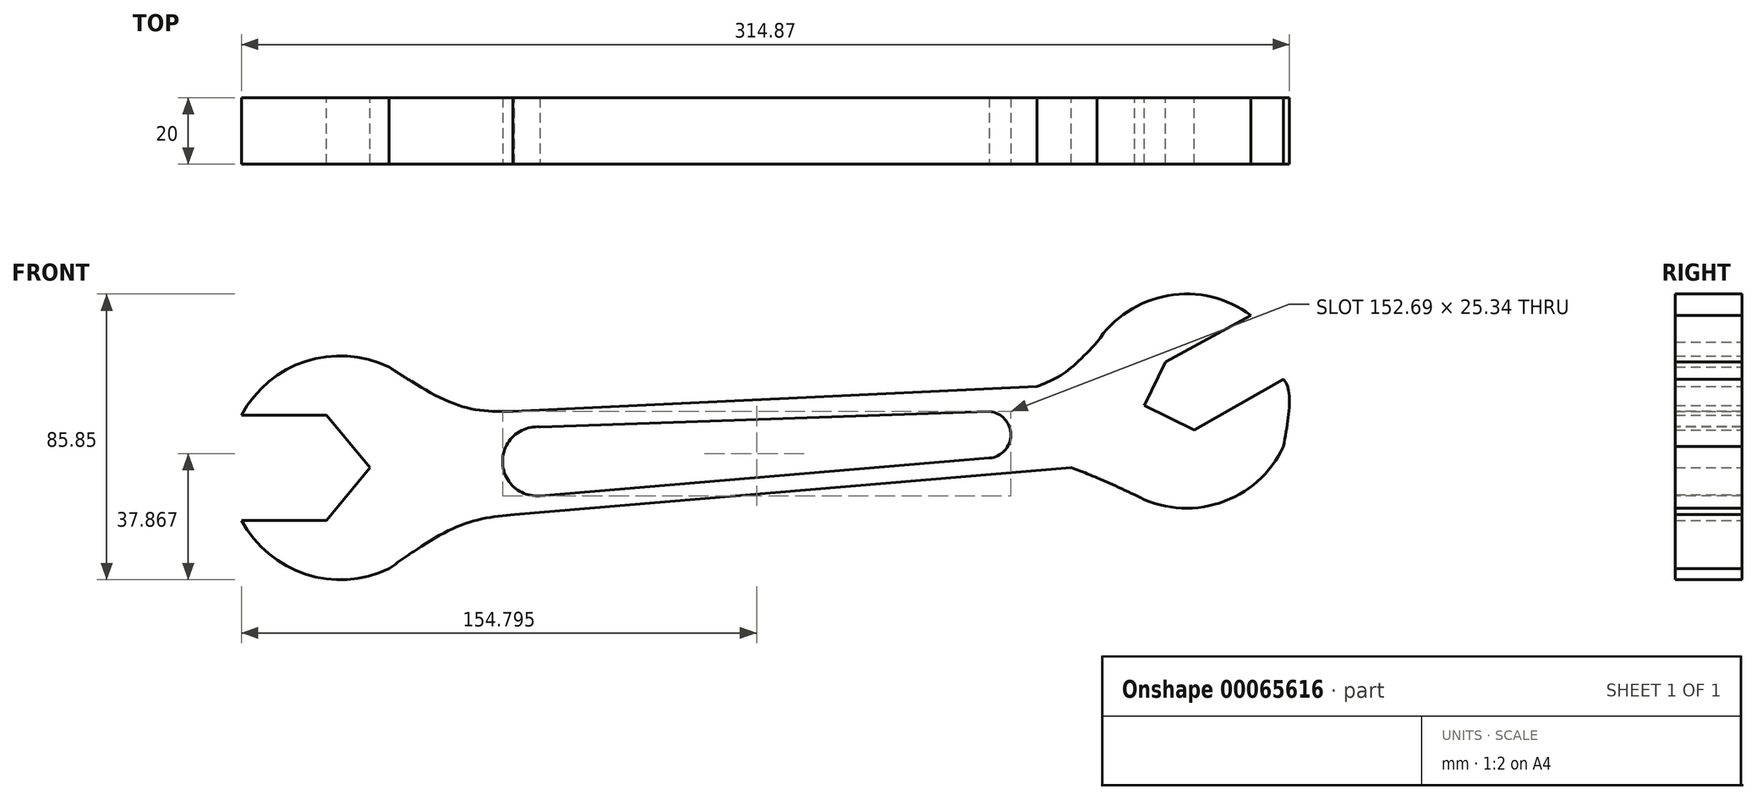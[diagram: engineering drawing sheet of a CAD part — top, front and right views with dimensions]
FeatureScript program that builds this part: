
annotation { "Feature Type Name" : "Feature", "Feature Type Description" : "" }
export const myFeature = defineFeature(function(context is Context, id is Id, definition is map)
    precondition{}
    {
        {
            var Q0;
            Q0=qCreatedBy(makeId("Front.planeOp"),FACE);
            var sketch = newSketch(context, id + "F0", { "sketchPlane" : qUnion([Q0])});
            skLineSegment(sketch, "E0", {"start": v(-115.15, 15.74) * mm, "end": v(-89.65, 15.74) * mm});
            skLineSegment(sketch, "E1", {"start": v(-89.65, 15.74) * mm, "end": v(-76.58, 0) * mm});
            skLineSegment(sketch, "E2", {"start": v(-76.58, 0) * mm, "end": v(-89.65, -15.82) * mm});
            skLineSegment(sketch, "E3", {"start": v(-89.65, -15.82) * mm, "end": v(-115.15, -15.82) * mm});
            skArc(sketch, "E4", {"start": v(-115.15, -15.82) * mm, "mid": v(-51.82, -0.04) * mm, "end": v(-115.15, 15.74) * mm});
            skFitSpline(sketch, "E5", {"points": [v(-70.8, 30.24) * mm, v(-49.2, 18.47) * mm, v(-33.55, 16.87) * mm], "startDerivative": vector(39.91, -26.01) * mm, "endDerivative": vector(34.43, 0.28) * mm});
            skFitSpline(sketch, "E6", {"points": [v(-70.8, -30.31) * mm, v(-49.2, -17.27) * mm, v(-33.14, -14.06) * mm], "startDerivative": vector(39.83, 28.07) * mm, "endDerivative": vector(35.33, 3.55) * mm});
            skLineSegment(sketch, "E7", {"start": v(-33.55, 16.87) * mm, "end": v(123.81, 24.33) * mm});
            skLineSegment(sketch, "E8", {"start": v(-33.14, -14.06) * mm, "end": v(134.1, 0) * mm});
            skArc(sketch, "E9", {"start": v(188.1, 45.74) * mm, "mid": v(137.57, 12.2) * mm, "end": v(197.94, 6.34) * mm});
            skLineSegment(sketch, "E10", {"start": v(188.1, 45.74) * mm, "end": v(162.5, 31.79) * mm});
            skLineSegment(sketch, "E11", {"start": v(162.5, 31.79) * mm, "end": v(156.1, 18.62) * mm});
            skPoint(sketch, "E12.endSnap0", {"position": v(159.3, 25.2) * mm});
            skLineSegment(sketch, "E13", {"start": v(156.1, 18.62) * mm, "end": v(171.07, 11.35) * mm});
            skLineSegment(sketch, "E14", {"start": v(171.07, 11.35) * mm, "end": v(197.94, 26.52) * mm});
            skFitSpline(sketch, "E15", {"points": [v(197.94, 6.34) * mm, v(197.94, 26.52) * mm, v(183.57, 26.52) * mm], "startDerivative": vector(8.52, 47.3) * mm, "endDerivative": vector(-38.6, -8.52) * mm});
            skFitSpline(sketch, "E16", {"points": [v(123.81, 24.33) * mm, v(132.02, 28.4) * mm, v(141.92, 37.7) * mm], "startDerivative": vector(18.25, 7.22) * mm, "endDerivative": vector(17.9, 19.16) * mm});
            skFitSpline(sketch, "E17", {"points": [v(134.1, 0) * mm, v(141.43, -2.83) * mm, v(153.2, -8.15) * mm], "startDerivative": vector(15.81, -5.75) * mm, "endDerivative": vector(22.01, -10.55) * mm});
            skSolve(sketch);
        }
        {
            var Q0;
            {var subQ5=sQuery(id+"F0.wireOp",EDGE,"E0");Q0=makeQuery(id+"F0.imprint","IMPRINT",FACE,{"disambiguationData":[TD([[makeQuery(id+"F0.imprint","IMPRINT",EDGE,{"derivedFrom":subQ5}),1.0]])]});}
            var Q1;
            {var subQ0=sQuery(id+"F0.wireOp",EDGE,"E7");Q1=makeQuery(id+"F0.imprint","IMPRINT",FACE,{"disambiguationData":[TD([[makeQuery(id+"F0.imprint","IMPRINT",EDGE,{"derivedFrom":subQ0}),-1.0]])]});}
            var Q2;
            {var subQ0=sQuery(id+"F0.wireOp",EDGE,"E10");Q2=makeQuery(id+"F0.imprint","IMPRINT",FACE,{"disambiguationData":[TD([[makeQuery(id+"F0.imprint","IMPRINT",EDGE,{"derivedFrom":subQ0}),-1.0]])]});}
            extrude(context, id + "F1", {"entities" : qUnion([Q0, Q1, Q2]), "depth" : 20 * mm});
        }
        {
            var Q0;
            Q0=makeQuery(id+"F1.opExtrude","CAP_FACE",FACE,{"disambiguationData":[OSD([sQuery(id+"F0.wireOp",EDGE,"E0"),sQuery(id+"F0.wireOp",EDGE,"E1"),sQuery(id+"F0.wireOp",EDGE,"E2"),sQuery(id+"F0.wireOp",EDGE,"E3"),sQuery(id+"F0.wireOp",EDGE,"E4"),sQuery(id+"F0.wireOp",EDGE,"E5"),sQuery(id+"F0.wireOp",EDGE,"E6"),sQuery(id+"F0.wireOp",EDGE,"E7"),sQuery(id+"F0.wireOp",EDGE,"E8"),sQuery(id+"F0.wireOp",EDGE,"E9"),sQuery(id+"F0.wireOp",EDGE,"E10"),sQuery(id+"F0.wireOp",EDGE,"E11"),sQuery(id+"F0.wireOp",EDGE,"E13"),sQuery(id+"F0.wireOp",EDGE,"E14"),sQuery(id+"F0.wireOp",EDGE,"E15"),sQuery(id+"F0.wireOp",EDGE,"E16"),sQuery(id+"F0.wireOp",EDGE,"E17")])],"isStart":false});
            var sketch = newSketch(context, id + "F2", { "sketchPlane" : qUnion([Q0])});
            skLineSegment(sketch, "E18", {"start": v(-25.44, 12.23) * mm, "end": v(109.56, 16.87) * mm});
            skLineSegment(sketch, "E19", {"start": v(-25.44, -8.47) * mm, "end": v(109.56, 2.88) * mm});
            skArc(sketch, "E20", {"start": v(109.56, 2.88) * mm, "mid": v(115.99, 9.87) * mm, "end": v(109.56, 16.87) * mm});
            skArc(sketch, "E21", {"start": v(-25.44, 12.23) * mm, "mid": v(-36.7, 1.88) * mm, "end": v(-25.44, -8.47) * mm});
            skSolve(sketch);
        }
        {
            var Q0;
            Q0=makeQuery(id+"F2.imprint","IMPRINT",FACE,{"disambiguationData":[TD([[makeQuery(id+"F2.imprint","IMPRINT",EDGE,{"derivedFrom":sQuery(id+"F2.wireOp",EDGE,"E18")}),-1.0]])]});
            extrude(context, id + "F3", {"entities" : qUnion([Q0]), "operationType" : NewBodyOperationType.REMOVE, "oppositeDirection" : true, "depth" : 25 * mm});
        }
    });
